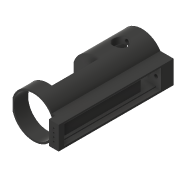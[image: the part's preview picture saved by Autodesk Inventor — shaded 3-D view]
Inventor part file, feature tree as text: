
AUTODESK INVENTOR PART (.ipt)
format: ipt  version: 2017 (Build 210142000, 142)  size: 556,544 bytes
history: native  units: in
note: dims shown in document units (in); Inventor stores cm internally (conversion verified against a paired STEP export)
features: extrude x41, sketch x41, reference x19, projected_geometry x18, other x8, chamfer x2, plane x1
ambient origin geometry x8: Origin, YZ Plane, XZ Plane, XY Plane, X Axis, Y Axis, Z Axis, Center Point
bodies: Solid1 (feature_tree)
feature tree (130):
  extrude  "Extrusion1"  Depth=0.75in
  extrude  "Extrusion2"  Depth=1.0in
  extrude  "Extrusion3"  Depth=1.125in
  extrude  "Extrusion4"  Depth=0.75in
  extrude  "Extrusion5"  Depth=0.1in TaperAngle=0.0deg
  extrude  "Extrusion6"  Depth=0.375in TaperAngle=0.0deg
  extrude  "Extrusion7"  Depth=0.5in TaperAngle=0.0deg
  extrude  "Extrusion8"  Depth=0.125in TaperAngle=0.0deg
  extrude  "Extrusion9"  Depth=0.05in
  extrude  "Extrusion10"  Depth=2.5in
  extrude  "Extrusion11"  Depth=0.125in TaperAngle=0.0deg
  sketch  "Sketch12"  dims[d36=0.125in d37=0.0in d38=0.125in d39=0.0in]
  other  "Work Point1"
  extrude  "Extrusion12"  Depth=0.125in TaperAngle=0.0deg
  extrude  "Extrusion13"  Depth=0.125in TaperAngle=0.0deg
  extrude  "Extrusion14"  Depth=0.125in
  extrude  "Extrusion15"  Depth=0.5in TaperAngle=0.0deg
  sketch  "Sketch16"  dims[d49=0.0in d50=0.0in d51=1.04in]
  plane  "Work Plane1"
  extrude  "Extrusion16"  Depth=1.04in
  extrude  "Extrusion17"  Depth=0.79in
  extrude  "Extrusion18"  Depth=0.125in TaperAngle=45.0deg
  extrude  "Extrusion19"  Depth=2.625in TaperAngle=0.0deg
  extrude  "Extrusion20"  Depth=1.5in TaperAngle=0.0deg
  chamfer  "Chamfer1"  Distance=1.5in
  extrude  "Extrusion21"  Depth=0.1in TaperAngle=0.0deg
  chamfer  "Chamfer2"  Distance=0.1in
  extrude  "Extrusion22"  Depth=0.0625in
  extrude  "Extrusion23"  Depth=3.0in TaperAngle=0.0deg
  extrude  "Extrusion24"  Depth=0.0625in TaperAngle=0.0deg
  extrude  "Extrusion25"  Depth=0.375in
  extrude  "Extrusion26"  Depth=0.0625in TaperAngle=0.0deg
  extrude  "Extrusion27"  Depth=0.5in TaperAngle=0.0deg
  extrude  "Extrusion28"  Depth=0.1in
  extrude  "Extrusion29"  Depth=0.1in
  extrude  "Extrusion30"  Depth=0.5in TaperAngle=0.0deg
  extrude  "Extrusion31"  Depth=1.0in TaperAngle=0.0deg
  extrude  "Extrusion32"  Depth=1.0in TaperAngle=0.0deg
  extrude  "Extrusion33"  [1 undecoded]
  extrude  "Extrusion34"  [1 undecoded]
  extrude  "Extrusion35"  [1 undecoded]
  extrude  "Extrusion36"  [1 undecoded]
  extrude  "Extrusion37"  [1 undecoded]
  extrude  "Extrusion38"  [1 undecoded]
  extrude  "Extrusion39"  [1 undecoded]
  extrude  "Extrusion40"  [1 undecoded]
  extrude  "Extrusion41"  [1 undecoded]
  sketch  "Sketch1"  dims[d0=1.0in d1=0.75in]
  sketch  "Sketch2"  dims[d2=1.0in d3=0.5in d4=0.0in d5=0.0in d6=1.0in]
  sketch  "Sketch3"  dims[d7=0.125in d8=0.0in d9=1.125in]
  sketch  "Sketch4"  dims[d10=2.625in d11=0.0in d12=0.75in]
  sketch  "Sketch5"  dims[d13=0.75in d14=0.1in d15=0.0in]
  reference  "Reference1"
  reference  "Reference2"
  reference  "Reference3"
  reference  "Reference4"
  reference  "Reference5"
  sketch  "Sketch6"  dims[d16=2.625in d17=0.0in d18=0.375in d19=0.0in]
  reference  "Reference6"
  sketch  "Sketch7"  dims[d20=0.1in d21=0.0in d22=0.5in d23=0.0in]
  projected_geometry  "Projected Loop1"
  sketch  "Sketch8"  dims[d24=0.0in d25=0.0in d26=0.125in d27=0.0in]
  sketch  "Sketch9"  dims[d28=0.0in d29=0.05in]
  projected_geometry  "Projected Loop2"
  sketch  "Sketch10"  dims[d30=0.05in d31=2.5in]
  sketch  "Sketch11"  dims[d32=0.125in d33=0.0in d34=0.125in d35=0.0in]
  projected_geometry  "Projected Loop3"
  reference  "Reference7"
  reference  "Reference8"
  projected_geometry  "Projected Loop4"
  projected_geometry  "Projected Loop5"
  sketch  "Sketch13"  dims[d40=0.125in d41=0.0in d42=0.125in d43=0.0in]
  sketch  "Sketch14"  dims[d44=0.25in d45=0.125in]
  reference  "Reference9"
  reference  "Reference10"
  reference  "Reference11"
  reference  "Reference12"
  sketch  "Sketch15"  dims[d46=0.0in d47=0.5in d48=0.0in]
  reference  "Reference13"
  reference  "Reference14"
  reference  "Reference15"
  reference  "Reference16"
  sketch  "Sketch17"  dims[d52=0.5in d53=0.0in d54=0.79in]
  projected_geometry  "Projected Loop6"
  sketch  "Sketch18"  dims[d55=0.5in d56=0.0in d57=0.125in d58=0.125in d59=45.0deg]
  sketch  "Sketch19"  dims[d60=0.2in d61=0.0in d62=2.625in d63=0.0in]
  sketch  "Sketch20"  dims[d64=0.125in d65=0.125in d66=45.0deg d67=1.5in d68=0.0in]
  sketch  "Sketch21"  dims[d69=0.0625in d70=1.5in d71=0.0in]
  projected_geometry  "Projected Loop7"
  sketch  "Sketch22"  dims[d72=1.5in d73=0.0in d74=0.1in d75=0.0in]
  projected_geometry  "Projected Loop8"
  sketch  "Sketch23"  dims[d76=0.2835in d77=0.1in d78=0.0in]
  reference  "Reference17"
  sketch  "Sketch24"  dims[d79=0.1in d80=0.0in d81=0.0625in]
  projected_geometry  "Projected Loop9"
  projected_geometry  "Projected Loop10"
  projected_geometry  "Projected Loop11"
  sketch  "Sketch25"  dims[d82=3.0in d83=0.0in d84=3.0in d85=0.0in]
  sketch  "Sketch26"  dims[d86=0.2835in d87=0.0625in d88=0.0in]
  reference  "Reference18"
  sketch  "Sketch27"  dims[d89=0.0625in d90=0.0in d91=0.375in]
  sketch  "Sketch28"  dims[d92=0.0625in d93=0.0in d94=0.0625in d95=0.0in]
  sketch  "Sketch29"  dims[d96=0.5in d97=0.0in d98=0.5in d99=0.0in]
  projected_geometry  "Projected Loop12"
  sketch  "Sketch30"  dims[d100=0.5in d101=0.0in d102=0.1in]
  sketch  "Sketch31"  dims[d103=0.1in d104=0.1in]
  projected_geometry  "Projected Loop13"
  sketch  "Sketch32"  dims[d105=0.125in d106=0.5in d107=0.0in]
  sketch  "Sketch33"  dims[d108=0.5in d109=0.0in d110=1.0in d111=0.0in]
  projected_geometry  "Projected Loop14"
  sketch  "Sketch34"  dims[d112=1.0in d113=0.0in d114=1.0in d115=0.0in]
  projected_geometry  "Projected Loop15"
  sketch  "Sketch35"
  sketch  "Sketch36"
  projected_geometry  "Projected Loop16"
  sketch  "Sketch37"
  sketch  "Sketch38"
  sketch  "Sketch39"
  reference  "Reference19"
  sketch  "Sketch40"
  sketch  "Sketch41"
  projected_geometry  "Projected Loop17"
  projected_geometry  "Projected Loop18"
  parser-record x1  (decoder bookkeeping rows leaked as tree rows — omitted from the tree; the rows remain in map.json)
  other  "Assembly1.iam"
  other  "Heater Holder:1"
  other  "Header Holder Test:1"
  other  "Vial:1"
  other  "Bottom Assembly:1"
  other  "Led Holder:1"
note: 9 required parameter values undecoded (feature->parameter linkage not recoverable at this tier; creation-order binding heuristic only, values carry confidence <= 0.55)
note: 1 file-system path scrubbed to <path> (originals preserved in map.json)
